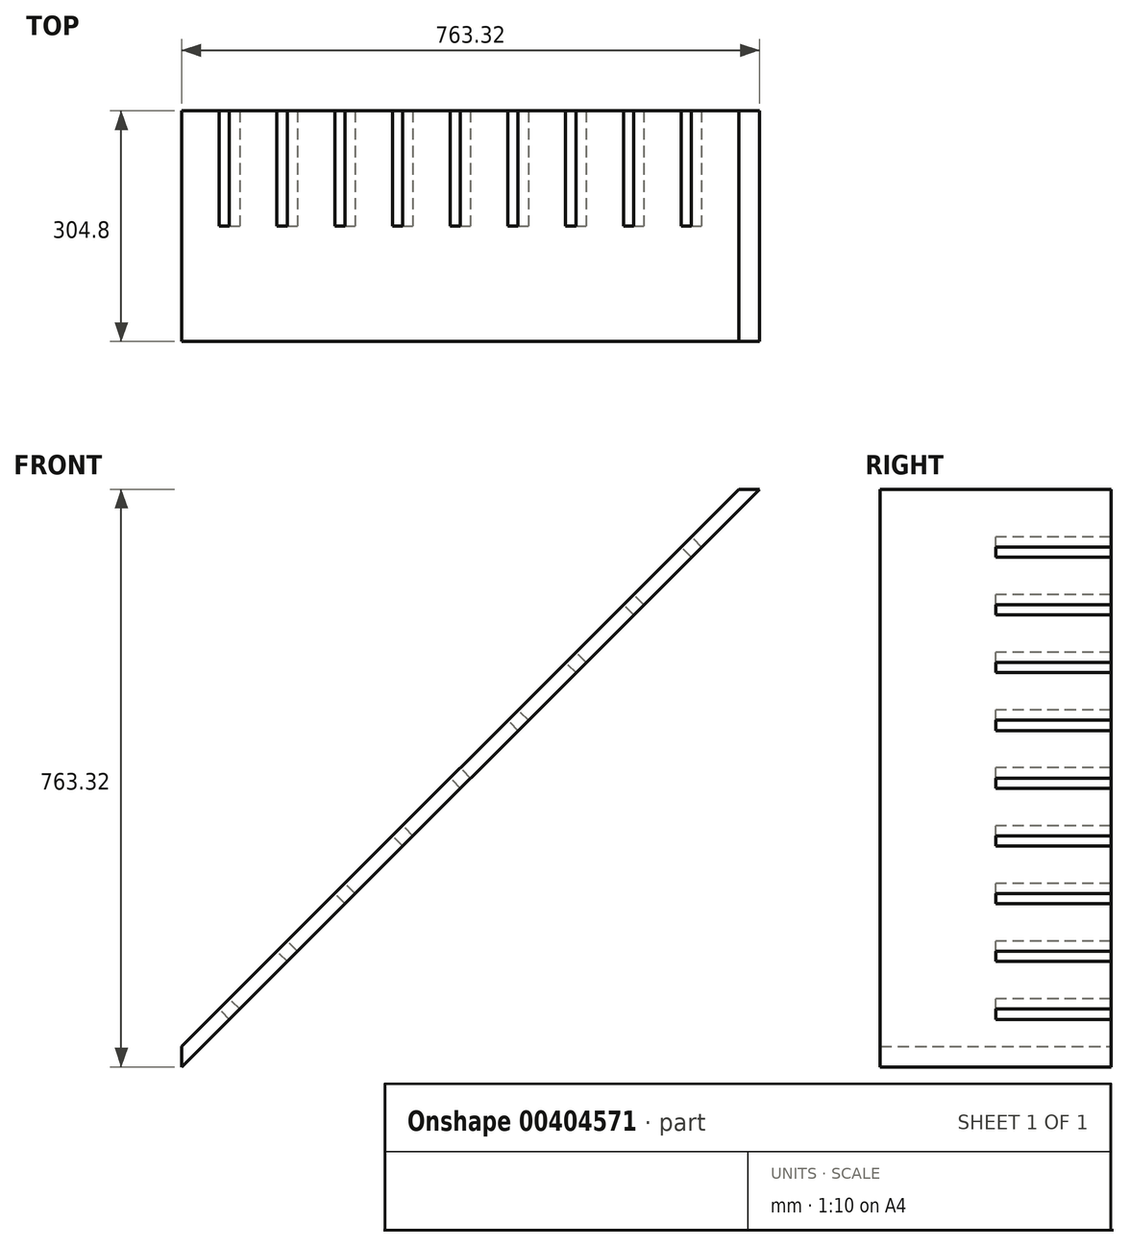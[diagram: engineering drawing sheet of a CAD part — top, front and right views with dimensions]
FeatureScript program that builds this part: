
annotation { "Feature Type Name" : "Feature", "Feature Type Description" : "" }
export const myFeature = defineFeature(function(context is Context, id is Id, definition is map)
    precondition{}
    {
        {
            var Q0;
            Q0=qCreatedBy(makeId("Front.planeOp"),FACE);
            var sketch = newSketch(context, id + "F0", { "sketchPlane" : qUnion([Q0])});
            skLineSegment(sketch, "E0.left", {"start": v(-421.52, 0) * mm, "end": v(-421.52, 26.94) * mm});
            skPoint(sketch, "E0.middle", {"position": v(22.97, 488.94) * mm});
            skLineSegment(sketch, "E1", {"start": v(-421.52, 0) * mm, "end": v(341.8, 763.32) * mm});
            skLineSegment(sketch, "E2", {"start": v(-421.52, 26.94) * mm, "end": v(314.86, 763.32) * mm});
            skLineSegment(sketch, "E3", {"start": v(341.8, 763.32) * mm, "end": v(314.86, 763.32) * mm});
            skSolve(sketch);
        }
        {
            var Q0;
            Q0=qSketchRegion(id+"F0",true);
            extrude(context, id + "F1", {"entities" : qUnion([Q0]), "endBound" : BoundingType.SYMMETRIC, "depth" : 304.8 * mm});
        }
        {
            var Q0;
            Q0=makeQuery(id+"F1.opExtrude","SWEPT_FACE",FACE,{"disambiguationData":[OSD([sQuery(id+"F0.wireOp",EDGE,"E2")])]});
            var sketch = newSketch(context, id + "F2", { "sketchPlane" : qUnion([Q0])});
            skLineSegment(sketch, "E4.bottom", {"start": v(-152.4, -209.16) * mm, "end": v(0, -209.16) * mm});
            skLineSegment(sketch, "E4.top", {"start": v(-152.4, -190.11) * mm, "end": v(0, -190.11) * mm});
            skLineSegment(sketch, "E4.left", {"start": v(-152.4, -209.16) * mm, "end": v(-152.4, -190.11) * mm});
            skLineSegment(sketch, "E4.right", {"start": v(0, -209.16) * mm, "end": v(0, -190.11) * mm});
            skLineSegment(sketch, "E5.bottom", {"start": v(-152.4, -101.21) * mm, "end": v(0, -101.21) * mm});
            skLineSegment(sketch, "E5.top", {"start": v(-152.4, -82.16) * mm, "end": v(0, -82.16) * mm});
            skLineSegment(sketch, "E5.left", {"start": v(-152.4, -101.21) * mm, "end": v(-152.4, -82.16) * mm});
            skLineSegment(sketch, "E5.right", {"start": v(0, -101.21) * mm, "end": v(0, -82.16) * mm});
            skLineSegment(sketch, "E6.bottom", {"start": v(-152.4, 6.74) * mm, "end": v(0, 6.74) * mm});
            skLineSegment(sketch, "E6.top", {"start": v(-152.4, 25.79) * mm, "end": v(0, 25.79) * mm});
            skLineSegment(sketch, "E6.left", {"start": v(-152.4, 6.74) * mm, "end": v(-152.4, 25.79) * mm});
            skLineSegment(sketch, "E6.right", {"start": v(0, 6.74) * mm, "end": v(0, 25.79) * mm});
            skLineSegment(sketch, "E7.bottom", {"start": v(-152.4, 114.69) * mm, "end": v(0, 114.69) * mm});
            skLineSegment(sketch, "E7.top", {"start": v(-152.4, 133.74) * mm, "end": v(0, 133.74) * mm});
            skLineSegment(sketch, "E7.left", {"start": v(-152.4, 114.69) * mm, "end": v(-152.4, 133.74) * mm});
            skLineSegment(sketch, "E7.right", {"start": v(0, 114.69) * mm, "end": v(0, 133.74) * mm});
            skLineSegment(sketch, "E8.bottom", {"start": v(-152.4, 222.64) * mm, "end": v(0, 222.64) * mm});
            skLineSegment(sketch, "E8.top", {"start": v(-152.4, 241.69) * mm, "end": v(0, 241.69) * mm});
            skLineSegment(sketch, "E8.left", {"start": v(-152.4, 222.64) * mm, "end": v(-152.4, 241.69) * mm});
            skLineSegment(sketch, "E8.right", {"start": v(0, 222.64) * mm, "end": v(0, 241.69) * mm});
            skLineSegment(sketch, "E9.bottom", {"start": v(-152.4, 330.59) * mm, "end": v(0, 330.59) * mm});
            skLineSegment(sketch, "E9.top", {"start": v(-152.4, 349.64) * mm, "end": v(0, 349.64) * mm});
            skLineSegment(sketch, "E9.left", {"start": v(-152.4, 330.59) * mm, "end": v(-152.4, 349.64) * mm});
            skLineSegment(sketch, "E9.right", {"start": v(0, 330.59) * mm, "end": v(0, 349.64) * mm});
            skLineSegment(sketch, "E10.bottom", {"start": v(-152.4, 438.54) * mm, "end": v(0, 438.54) * mm});
            skLineSegment(sketch, "E10.top", {"start": v(-152.4, 457.59) * mm, "end": v(0, 457.59) * mm});
            skLineSegment(sketch, "E10.left", {"start": v(-152.4, 438.54) * mm, "end": v(-152.4, 457.59) * mm});
            skLineSegment(sketch, "E10.right", {"start": v(0, 438.54) * mm, "end": v(0, 457.59) * mm});
            skLineSegment(sketch, "E11.bottom", {"start": v(-152.4, 546.49) * mm, "end": v(0, 546.49) * mm});
            skLineSegment(sketch, "E11.top", {"start": v(-152.4, 565.54) * mm, "end": v(0, 565.54) * mm});
            skLineSegment(sketch, "E11.left", {"start": v(-152.4, 546.49) * mm, "end": v(-152.4, 565.54) * mm});
            skLineSegment(sketch, "E11.right", {"start": v(0, 546.49) * mm, "end": v(0, 565.54) * mm});
            skLineSegment(sketch, "E12.bottom", {"start": v(-152.4, 654.44) * mm, "end": v(0, 654.44) * mm});
            skLineSegment(sketch, "E12.top", {"start": v(-152.4, 673.49) * mm, "end": v(0, 673.49) * mm});
            skLineSegment(sketch, "E12.left", {"start": v(-152.4, 654.44) * mm, "end": v(-152.4, 673.49) * mm});
            skLineSegment(sketch, "E12.right", {"start": v(0, 654.44) * mm, "end": v(0, 673.49) * mm});
            skSolve(sketch);
        }
        {
            var Q0;
            Q0=qSketchRegion(id+"F2",true);
            extrude(context, id + "F3", {"entities" : qUnion([Q0]), "operationType" : NewBodyOperationType.REMOVE, "oppositeDirection" : true, "depth" : 19.05 * mm});
        }
    });
